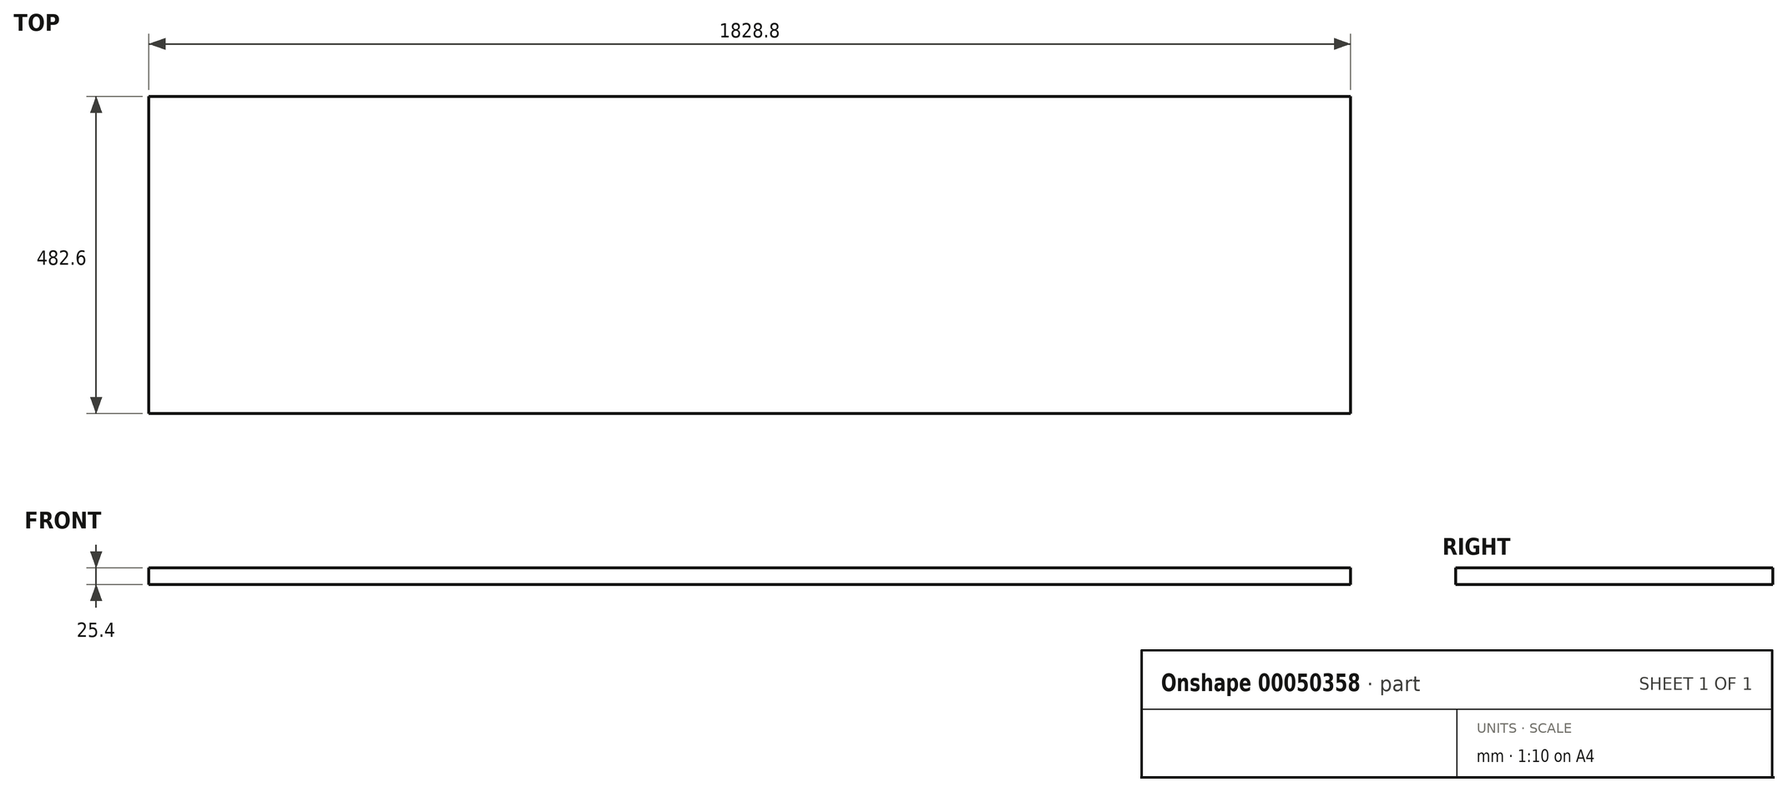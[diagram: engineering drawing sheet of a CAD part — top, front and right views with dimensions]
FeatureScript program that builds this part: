
annotation { "Feature Type Name" : "Feature", "Feature Type Description" : "" }
export const myFeature = defineFeature(function(context is Context, id is Id, definition is map)
    precondition{}
    {
        {
            var Q0;
            Q0=qCreatedBy(makeId("Top.planeOp"),FACE);
            var sketch = newSketch(context, id + "F0", { "sketchPlane" : qUnion([Q0])});
            skLineSegment(sketch, "E0.bottom", {"start": v(-746.92, 231.65) * mm, "end": v(1081.88, 231.65) * mm});
            skLineSegment(sketch, "E0.top", {"start": v(-746.92, -250.95) * mm, "end": v(1081.88, -250.95) * mm});
            skLineSegment(sketch, "E0.left", {"start": v(-746.92, 231.65) * mm, "end": v(-746.92, -250.95) * mm});
            skLineSegment(sketch, "E0.right", {"start": v(1081.88, 231.65) * mm, "end": v(1081.88, -250.95) * mm});
            skSolve(sketch);
        }
        {
            var Q0;
            Q0=makeQuery(id+"F0.imprint","IMPRINT",FACE,{"disambiguationData":[TD([[makeQuery(id+"F0.imprint","IMPRINT",EDGE,{"derivedFrom":sQuery(id+"F0.wireOp",EDGE,"E0.bottom")}),-1.0]])]});
            extrude(context, id + "F1", {"entities" : qUnion([Q0]), "depth" : 25.4 * mm});
        }
    });
